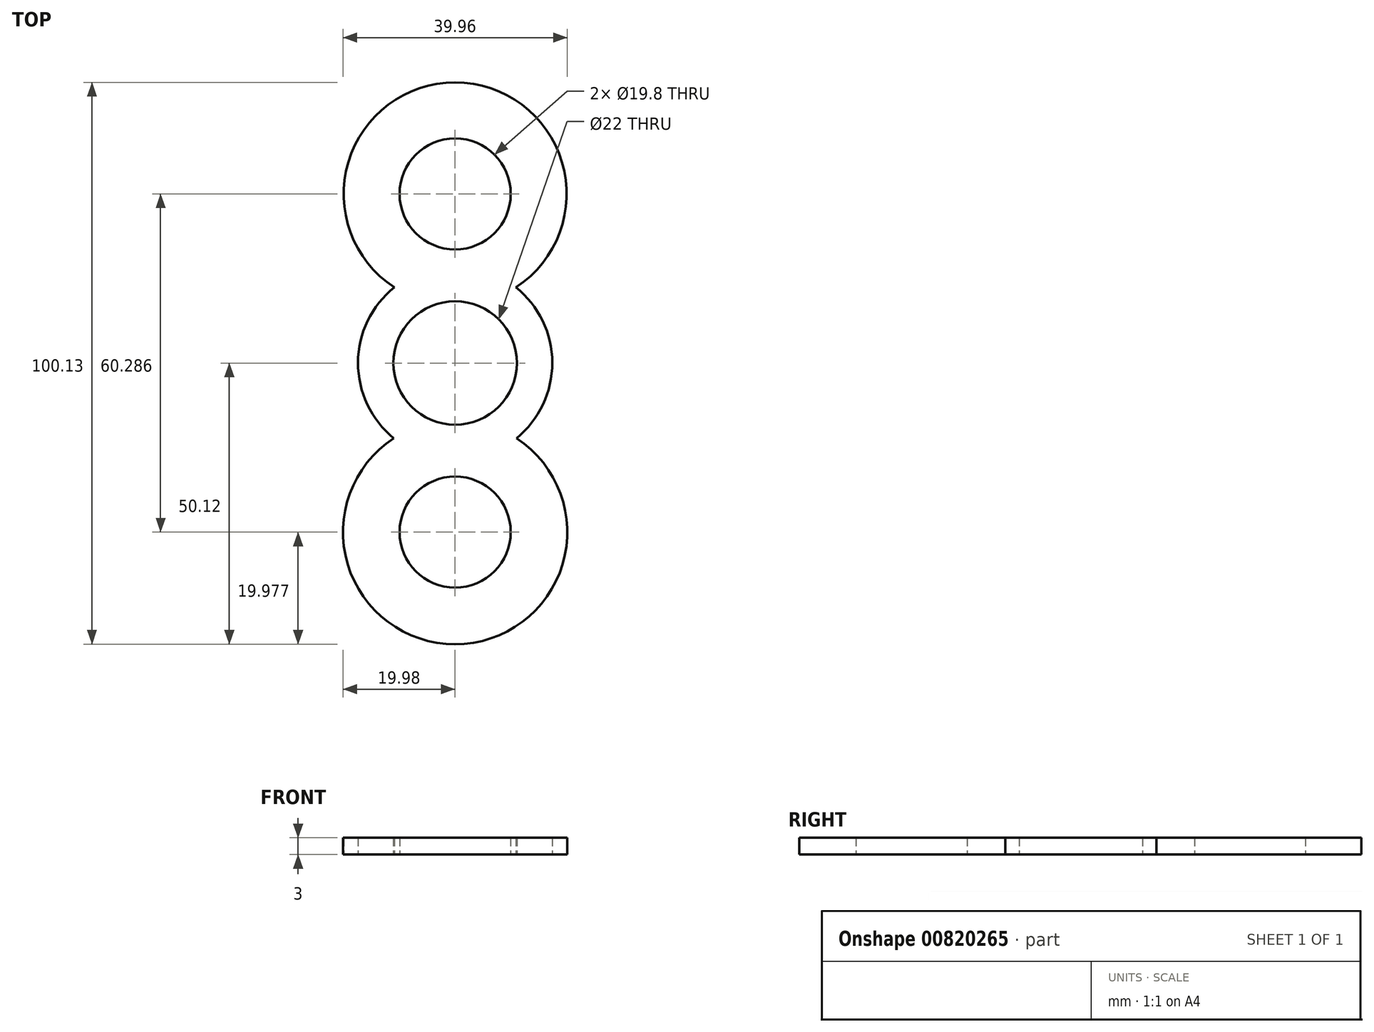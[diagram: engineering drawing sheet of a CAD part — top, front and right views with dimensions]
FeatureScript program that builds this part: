
annotation { "Feature Type Name" : "Feature", "Feature Type Description" : "" }
export const myFeature = defineFeature(function(context is Context, id is Id, definition is map)
    precondition{}
    {
        {
            var Q0;
            Q0=qCreatedBy(makeId("Top.planeOp"),FACE);
            var sketch = newSketch(context, id + "F0", { "sketchPlane" : qUnion([Q0])});
            skCircle(sketch, "E0", {"center": v(0, 30.14) * mm, "radius": 9.9 * mm});
            skCircle(sketch, "E1", {"center": v(0, -30.14) * mm, "radius": 9.9 * mm});
            skArc(sketch, "E2", {"start": v(-10.93, -13.42) * mm, "mid": v(0, -50.12) * mm, "end": v(10.93, -13.42) * mm});
            skArc(sketch, "E3", {"start": v(-10.83, 13.5) * mm, "mid": v(-17.3, 0.06) * mm, "end": v(-10.93, -13.42) * mm});
            skArc(sketch, "E4.trimOffspring", {"start": v(10.83, 13.5) * mm, "mid": v(0, 50) * mm, "end": v(-10.83, 13.5) * mm});
            skArc(sketch, "E5.trimOffspring", {"start": v(10.93, -13.42) * mm, "mid": v(17.3, 0.06) * mm, "end": v(10.83, 13.5) * mm});
            skCircle(sketch, "E6", {"center": v(0, 0) * mm, "radius": 11 * mm});
            skSolve(sketch);
        }
        {
            var Q0;
            Q0=makeQuery(id+"F0.imprint","IMPRINT",FACE,{"disambiguationData":[TD([[makeQuery(id+"F0.imprint","IMPRINT",EDGE,{"derivedFrom":sQuery(id+"F0.wireOp",EDGE,"E0")}),-1.0]])]});
            extrude(context, id + "F1", {"entities" : qUnion([Q0]), "depth" : 3 * mm, "offsetDistance" : 25 * mm});
        }
    });
